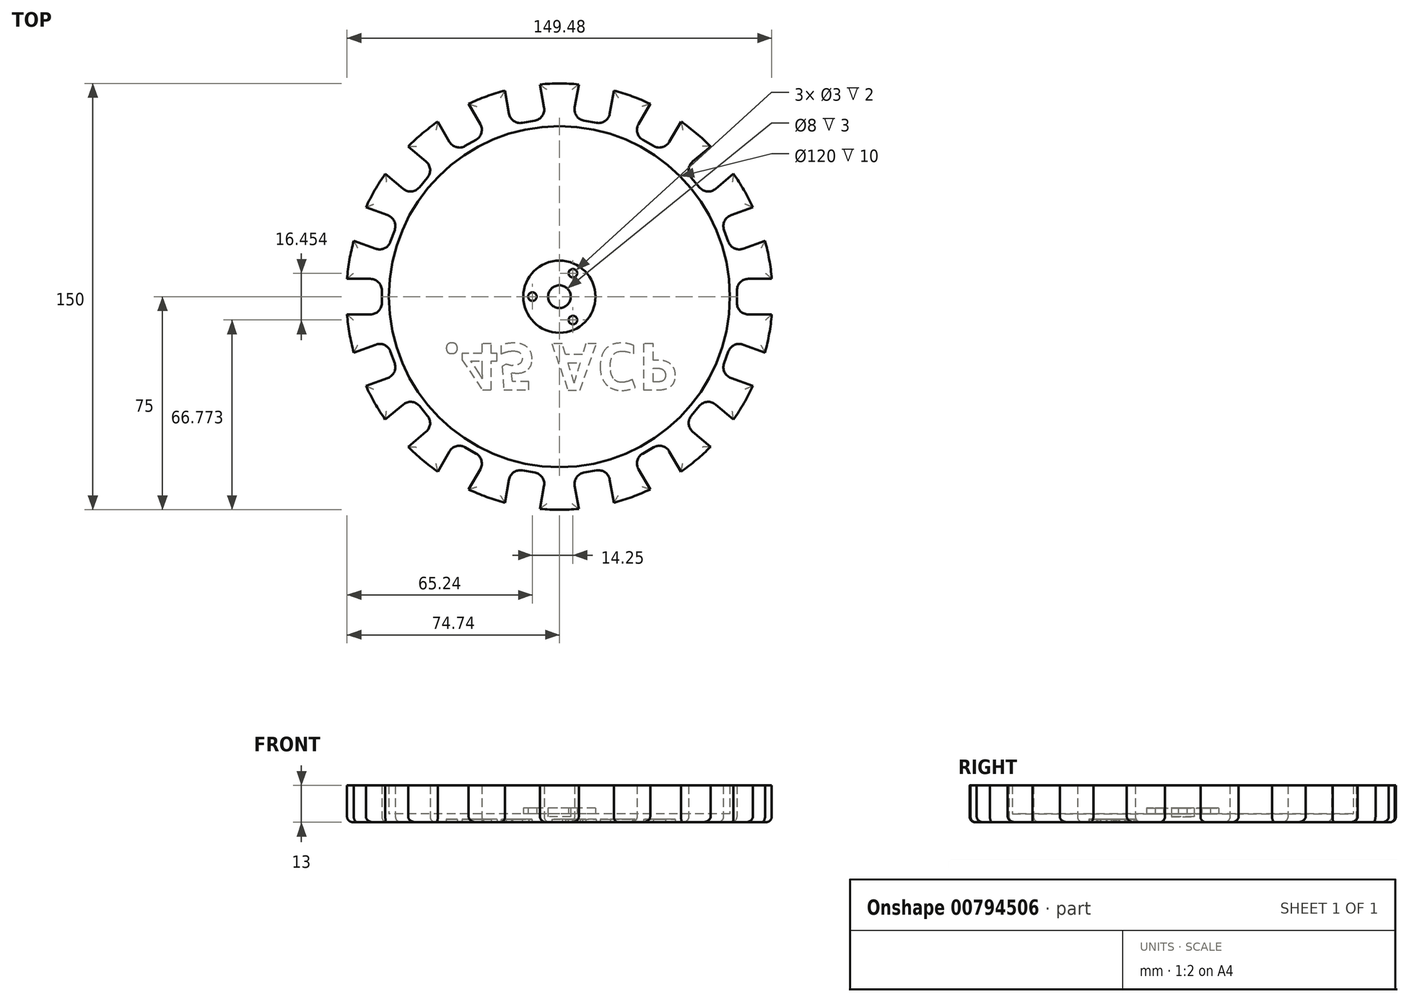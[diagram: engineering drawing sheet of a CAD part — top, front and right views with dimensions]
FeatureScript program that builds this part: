
annotation { "Feature Type Name" : "Feature", "Feature Type Description" : "" }
export const myFeature = defineFeature(function(context is Context, id is Id, definition is map)
    precondition{}
    {
        {
            var Q0;
            Q0=qCreatedBy(makeId("Top.planeOp"),FACE);
            var sketch = newSketch(context, id + "F0", { "sketchPlane" : qUnion([Q0])});
            skCircle(sketch, "E0", {"center": v(0, 0) * mm, "radius": 75 * mm});
            skCircle(sketch, "E1", {"center": v(0, 0) * mm, "radius": 60 * mm});
            skLineSegment(sketch, "E2", {"start": v(0, 0) * mm, "end": v(-124.02, 0) * mm, "construction": true});
            skPoint(sketch, "E3", {"position": v(-75, 0) * mm});
            skLineSegment(sketch, "E4.bottom", {"start": v(-75, -6.25) * mm, "end": v(-66.5, -6.25) * mm});
            skLineSegment(sketch, "E4.top", {"start": v(-75, 6.25) * mm, "end": v(-66.5, 6.25) * mm});
            skLineSegment(sketch, "E4.left", {"start": v(-75, -6.25) * mm, "end": v(-75, 6.25) * mm});
            skLineSegment(sketch, "E4.right", {"start": v(-62.5, -2.25) * mm, "end": v(-62.5, 2.25) * mm});
            skPoint(sketch, "E4.middle", {"position": v(-68.75, 0) * mm});
            skPoint(sketch, "E5.visualSharp", {"position": v(-62.5, 6.25) * mm});
            skArc(sketch, "E5.filletArc", {"start": v(-62.5, 2.25) * mm, "mid": v(-63.67, 5.08) * mm, "end": v(-66.5, 6.25) * mm});
            skPoint(sketch, "E6.visualSharp", {"position": v(-62.5, -6.25) * mm});
            skArc(sketch, "E6.filletArc", {"start": v(-66.5, -6.25) * mm, "mid": v(-63.67, -5.08) * mm, "end": v(-62.5, -2.25) * mm});
            skPoint(sketch, "E7.center", {"position": v(1.56, 0) * mm});
            skCircle(sketch, "E8", {"center": v(0, 0) * mm, "radius": 4 * mm});
            skCircle(sketch, "E9", {"center": v(0, 0) * mm, "radius": 12.7 * mm});
            skCircle(sketch, "E10", {"center": v(0, 0) * mm, "radius": 9.5 * mm, "construction": true});
            skCircle(sketch, "E11", {"center": v(-9.5, 0) * mm, "radius": 1.5 * mm});
            skCircle(sketch, "E12.1.0", {"center": v(-4.75, -8.23) * mm, "radius": 1.5 * mm});
            skCircle(sketch, "E12.2.0", {"center": v(4.75, -8.23) * mm, "radius": 1.5 * mm});
            skCircle(sketch, "E12.3.0", {"center": v(9.5, 0) * mm, "radius": 1.5 * mm});
            skCircle(sketch, "E12.4.0", {"center": v(4.75, 8.23) * mm, "radius": 1.5 * mm});
            skCircle(sketch, "E12.5.0", {"center": v(-4.75, 8.23) * mm, "radius": 1.5 * mm});
            skPoint(sketch, "E13.1.0", {"position": v(-60.87, -15.5) * mm});
            skPoint(sketch, "E13.1.1", {"position": v(-70.48, -25.65) * mm});
            skPoint(sketch, "E13.1.2", {"position": v(-56.6, -27.25) * mm});
            skPoint(sketch, "E13.1.3", {"position": v(-64.6, -23.51) * mm});
            skArc(sketch, "E13.1.4", {"start": v(-60.35, -28.62) * mm, "mid": v(-58.1, -26.55) * mm, "end": v(-57.96, -23.5) * mm});
            skArc(sketch, "E13.1.5", {"start": v(-59.5, -19.26) * mm, "mid": v(-61.57, -17) * mm, "end": v(-64.63, -16.87) * mm});
            skLineSegment(sketch, "E13.1.6", {"start": v(-68.34, -31.52) * mm, "end": v(-72.61, -19.78) * mm});
            skLineSegment(sketch, "E13.1.7", {"start": v(-57.96, -23.5) * mm, "end": v(-59.5, -19.26) * mm});
            skLineSegment(sketch, "E13.1.8", {"start": v(-72.61, -19.78) * mm, "end": v(-64.63, -16.87) * mm});
            skLineSegment(sketch, "E13.1.9", {"start": v(-68.34, -31.52) * mm, "end": v(-60.35, -28.62) * mm});
            skPoint(sketch, "E13.2.0", {"position": v(-51.9, -35.39) * mm});
            skPoint(sketch, "E13.2.1", {"position": v(-57.45, -48.2) * mm});
            skPoint(sketch, "E13.2.2", {"position": v(-43.86, -44.96) * mm});
            skPoint(sketch, "E13.2.3", {"position": v(-52.67, -44.2) * mm});
            skArc(sketch, "E13.2.4", {"start": v(-46.92, -47.53) * mm, "mid": v(-45.51, -44.82) * mm, "end": v(-46.43, -41.9) * mm});
            skArc(sketch, "E13.2.5", {"start": v(-49.32, -38.45) * mm, "mid": v(-52.04, -37.04) * mm, "end": v(-54.96, -37.96) * mm});
            skLineSegment(sketch, "E13.2.6", {"start": v(-53.44, -53) * mm, "end": v(-61.47, -43.42) * mm});
            skLineSegment(sketch, "E13.2.7", {"start": v(-46.43, -41.9) * mm, "end": v(-49.32, -38.45) * mm});
            skLineSegment(sketch, "E13.2.8", {"start": v(-61.47, -43.42) * mm, "end": v(-54.96, -37.96) * mm});
            skLineSegment(sketch, "E13.2.9", {"start": v(-53.44, -53) * mm, "end": v(-46.92, -47.53) * mm});
            skPoint(sketch, "E13.3.0", {"position": v(-36.66, -51) * mm});
            skPoint(sketch, "E13.3.1", {"position": v(-37.5, -64.95) * mm});
            skPoint(sketch, "E13.3.2", {"position": v(-25.84, -57.25) * mm});
            skPoint(sketch, "E13.3.3", {"position": v(-34.38, -59.54) * mm});
            skArc(sketch, "E13.3.4", {"start": v(-27.84, -60.72) * mm, "mid": v(-27.44, -57.68) * mm, "end": v(-29.3, -55.25) * mm});
            skArc(sketch, "E13.3.5", {"start": v(-33.2, -53) * mm, "mid": v(-36.23, -52.6) * mm, "end": v(-38.66, -54.47) * mm});
            skLineSegment(sketch, "E13.3.6", {"start": v(-32.09, -68.08) * mm, "end": v(-42.91, -61.83) * mm});
            skLineSegment(sketch, "E13.3.7", {"start": v(-29.3, -55.25) * mm, "end": v(-33.2, -53) * mm});
            skLineSegment(sketch, "E13.3.8", {"start": v(-42.91, -61.83) * mm, "end": v(-38.66, -54.47) * mm});
            skLineSegment(sketch, "E13.3.9", {"start": v(-32.09, -68.08) * mm, "end": v(-27.84, -60.72) * mm});
            skPoint(sketch, "E13.4.0", {"position": v(-17, -60.47) * mm});
            skPoint(sketch, "E13.4.1", {"position": v(-13.02, -73.86) * mm});
            skPoint(sketch, "E13.4.2", {"position": v(-4.7, -62.64) * mm});
            skPoint(sketch, "E13.4.3", {"position": v(-11.94, -67.7) * mm});
            skArc(sketch, "E13.4.4", {"start": v(-5.4, -66.58) * mm, "mid": v(-6.06, -63.59) * mm, "end": v(-8.64, -61.94) * mm});
            skArc(sketch, "E13.4.5", {"start": v(-13.07, -61.16) * mm, "mid": v(-16.06, -61.82) * mm, "end": v(-17.7, -64.4) * mm});
            skLineSegment(sketch, "E13.4.6", {"start": v(-6.87, -74.95) * mm, "end": v(-19.18, -72.78) * mm});
            skLineSegment(sketch, "E13.4.7", {"start": v(-8.64, -61.94) * mm, "end": v(-13.07, -61.16) * mm});
            skLineSegment(sketch, "E13.4.8", {"start": v(-19.18, -72.78) * mm, "end": v(-17.7, -64.4) * mm});
            skLineSegment(sketch, "E13.4.9", {"start": v(-6.87, -74.95) * mm, "end": v(-5.4, -66.58) * mm});
            skPoint(sketch, "E13.5.0", {"position": v(4.7, -62.64) * mm});
            skPoint(sketch, "E13.5.1", {"position": v(13.02, -73.86) * mm});
            skPoint(sketch, "E13.5.2", {"position": v(17, -60.47) * mm});
            skPoint(sketch, "E13.5.3", {"position": v(11.94, -67.7) * mm});
            skArc(sketch, "E13.5.4", {"start": v(17.7, -64.4) * mm, "mid": v(16.06, -61.82) * mm, "end": v(13.07, -61.16) * mm});
            skArc(sketch, "E13.5.5", {"start": v(8.64, -61.94) * mm, "mid": v(6.06, -63.59) * mm, "end": v(5.4, -66.58) * mm});
            skLineSegment(sketch, "E13.5.6", {"start": v(19.18, -72.78) * mm, "end": v(6.87, -74.95) * mm});
            skLineSegment(sketch, "E13.5.7", {"start": v(13.07, -61.16) * mm, "end": v(8.64, -61.94) * mm});
            skLineSegment(sketch, "E13.5.8", {"start": v(6.87, -74.95) * mm, "end": v(5.4, -66.58) * mm});
            skLineSegment(sketch, "E13.5.9", {"start": v(19.18, -72.78) * mm, "end": v(17.7, -64.4) * mm});
            skPoint(sketch, "E13.6.0", {"position": v(25.84, -57.25) * mm});
            skPoint(sketch, "E13.6.1", {"position": v(37.5, -64.95) * mm});
            skPoint(sketch, "E13.6.2", {"position": v(36.66, -51) * mm});
            skPoint(sketch, "E13.6.3", {"position": v(34.37, -59.54) * mm});
            skArc(sketch, "E13.6.4", {"start": v(38.66, -54.47) * mm, "mid": v(36.23, -52.6) * mm, "end": v(33.2, -53) * mm});
            skArc(sketch, "E13.6.5", {"start": v(29.3, -55.25) * mm, "mid": v(27.44, -57.68) * mm, "end": v(27.84, -60.72) * mm});
            skLineSegment(sketch, "E13.6.6", {"start": v(42.91, -61.83) * mm, "end": v(32.09, -68.08) * mm});
            skLineSegment(sketch, "E13.6.7", {"start": v(33.2, -53) * mm, "end": v(29.3, -55.25) * mm});
            skLineSegment(sketch, "E13.6.8", {"start": v(32.09, -68.08) * mm, "end": v(27.84, -60.72) * mm});
            skLineSegment(sketch, "E13.6.9", {"start": v(42.91, -61.83) * mm, "end": v(38.66, -54.47) * mm});
            skPoint(sketch, "E13.7.0", {"position": v(43.86, -44.96) * mm});
            skPoint(sketch, "E13.7.1", {"position": v(57.45, -48.2) * mm});
            skPoint(sketch, "E13.7.2", {"position": v(51.9, -35.39) * mm});
            skPoint(sketch, "E13.7.3", {"position": v(52.67, -44.2) * mm});
            skArc(sketch, "E13.7.4", {"start": v(54.96, -37.96) * mm, "mid": v(52.04, -37.04) * mm, "end": v(49.32, -38.45) * mm});
            skArc(sketch, "E13.7.5", {"start": v(46.43, -41.9) * mm, "mid": v(45.51, -44.82) * mm, "end": v(46.92, -47.53) * mm});
            skLineSegment(sketch, "E13.7.6", {"start": v(61.47, -43.42) * mm, "end": v(53.44, -53) * mm});
            skLineSegment(sketch, "E13.7.7", {"start": v(49.32, -38.45) * mm, "end": v(46.43, -41.9) * mm});
            skLineSegment(sketch, "E13.7.8", {"start": v(53.44, -53) * mm, "end": v(46.92, -47.53) * mm});
            skLineSegment(sketch, "E13.7.9", {"start": v(61.47, -43.42) * mm, "end": v(54.96, -37.96) * mm});
            skPoint(sketch, "E13.8.0", {"position": v(56.6, -27.25) * mm});
            skPoint(sketch, "E13.8.1", {"position": v(70.48, -25.65) * mm});
            skPoint(sketch, "E13.8.2", {"position": v(60.87, -15.5) * mm});
            skPoint(sketch, "E13.8.3", {"position": v(64.6, -23.51) * mm});
            skArc(sketch, "E13.8.4", {"start": v(64.63, -16.87) * mm, "mid": v(61.57, -17) * mm, "end": v(59.5, -19.26) * mm});
            skArc(sketch, "E13.8.5", {"start": v(57.96, -23.5) * mm, "mid": v(58.1, -26.55) * mm, "end": v(60.35, -28.62) * mm});
            skLineSegment(sketch, "E13.8.6", {"start": v(72.61, -19.78) * mm, "end": v(68.34, -31.52) * mm});
            skLineSegment(sketch, "E13.8.7", {"start": v(59.5, -19.26) * mm, "end": v(57.96, -23.5) * mm});
            skLineSegment(sketch, "E13.8.8", {"start": v(68.34, -31.52) * mm, "end": v(60.35, -28.62) * mm});
            skLineSegment(sketch, "E13.8.9", {"start": v(72.61, -19.78) * mm, "end": v(64.63, -16.87) * mm});
            skPoint(sketch, "E13.9.0", {"position": v(62.5, -6.25) * mm});
            skPoint(sketch, "E13.9.1", {"position": v(75, 0) * mm});
            skPoint(sketch, "E13.9.2", {"position": v(62.5, 6.25) * mm});
            skPoint(sketch, "E13.9.3", {"position": v(68.75, 0) * mm});
            skArc(sketch, "E13.9.4", {"start": v(66.5, 6.25) * mm, "mid": v(63.67, 5.08) * mm, "end": v(62.5, 2.25) * mm});
            skArc(sketch, "E13.9.5", {"start": v(62.5, -2.25) * mm, "mid": v(63.67, -5.08) * mm, "end": v(66.5, -6.25) * mm});
            skLineSegment(sketch, "E13.9.6", {"start": v(75, 6.25) * mm, "end": v(75, -6.25) * mm});
            skLineSegment(sketch, "E13.9.7", {"start": v(62.5, 2.25) * mm, "end": v(62.5, -2.25) * mm});
            skLineSegment(sketch, "E13.9.8", {"start": v(75, -6.25) * mm, "end": v(66.5, -6.25) * mm});
            skLineSegment(sketch, "E13.9.9", {"start": v(75, 6.25) * mm, "end": v(66.5, 6.25) * mm});
            skPoint(sketch, "E13.10.0", {"position": v(60.87, 15.5) * mm});
            skPoint(sketch, "E13.10.1", {"position": v(70.48, 25.65) * mm});
            skPoint(sketch, "E13.10.2", {"position": v(56.6, 27.25) * mm});
            skPoint(sketch, "E13.10.3", {"position": v(64.6, 23.51) * mm});
            skArc(sketch, "E13.10.4", {"start": v(60.35, 28.62) * mm, "mid": v(58.1, 26.55) * mm, "end": v(57.96, 23.5) * mm});
            skArc(sketch, "E13.10.5", {"start": v(59.5, 19.26) * mm, "mid": v(61.57, 17) * mm, "end": v(64.63, 16.87) * mm});
            skLineSegment(sketch, "E13.10.6", {"start": v(68.34, 31.52) * mm, "end": v(72.61, 19.78) * mm});
            skLineSegment(sketch, "E13.10.7", {"start": v(57.96, 23.5) * mm, "end": v(59.5, 19.26) * mm});
            skLineSegment(sketch, "E13.10.8", {"start": v(72.61, 19.78) * mm, "end": v(64.63, 16.87) * mm});
            skLineSegment(sketch, "E13.10.9", {"start": v(68.34, 31.52) * mm, "end": v(60.35, 28.62) * mm});
            skPoint(sketch, "E13.11.0", {"position": v(51.9, 35.39) * mm});
            skPoint(sketch, "E13.11.1", {"position": v(57.45, 48.2) * mm});
            skPoint(sketch, "E13.11.2", {"position": v(43.86, 44.96) * mm});
            skPoint(sketch, "E13.11.3", {"position": v(52.67, 44.2) * mm});
            skArc(sketch, "E13.11.4", {"start": v(46.92, 47.53) * mm, "mid": v(45.51, 44.82) * mm, "end": v(46.43, 41.9) * mm});
            skArc(sketch, "E13.11.5", {"start": v(49.32, 38.45) * mm, "mid": v(52.04, 37.04) * mm, "end": v(54.96, 37.96) * mm});
            skLineSegment(sketch, "E13.11.6", {"start": v(53.44, 53) * mm, "end": v(61.47, 43.42) * mm});
            skLineSegment(sketch, "E13.11.7", {"start": v(46.43, 41.9) * mm, "end": v(49.32, 38.45) * mm});
            skLineSegment(sketch, "E13.11.8", {"start": v(61.47, 43.42) * mm, "end": v(54.96, 37.96) * mm});
            skLineSegment(sketch, "E13.11.9", {"start": v(53.44, 53) * mm, "end": v(46.92, 47.53) * mm});
            skPoint(sketch, "E13.12.0", {"position": v(36.66, 51) * mm});
            skPoint(sketch, "E13.12.1", {"position": v(37.5, 64.95) * mm});
            skPoint(sketch, "E13.12.2", {"position": v(25.84, 57.25) * mm});
            skPoint(sketch, "E13.12.3", {"position": v(34.38, 59.54) * mm});
            skArc(sketch, "E13.12.4", {"start": v(27.84, 60.72) * mm, "mid": v(27.44, 57.68) * mm, "end": v(29.3, 55.25) * mm});
            skArc(sketch, "E13.12.5", {"start": v(33.2, 53) * mm, "mid": v(36.23, 52.6) * mm, "end": v(38.66, 54.47) * mm});
            skLineSegment(sketch, "E13.12.6", {"start": v(32.09, 68.08) * mm, "end": v(42.91, 61.83) * mm});
            skLineSegment(sketch, "E13.12.7", {"start": v(29.3, 55.25) * mm, "end": v(33.2, 53) * mm});
            skLineSegment(sketch, "E13.12.8", {"start": v(42.91, 61.83) * mm, "end": v(38.66, 54.47) * mm});
            skLineSegment(sketch, "E13.12.9", {"start": v(32.09, 68.08) * mm, "end": v(27.84, 60.72) * mm});
            skPoint(sketch, "E13.13.0", {"position": v(17, 60.47) * mm});
            skPoint(sketch, "E13.13.1", {"position": v(13.02, 73.86) * mm});
            skPoint(sketch, "E13.13.2", {"position": v(4.7, 62.64) * mm});
            skPoint(sketch, "E13.13.3", {"position": v(11.94, 67.7) * mm});
            skArc(sketch, "E13.13.4", {"start": v(5.4, 66.58) * mm, "mid": v(6.06, 63.59) * mm, "end": v(8.64, 61.94) * mm});
            skArc(sketch, "E13.13.5", {"start": v(13.07, 61.16) * mm, "mid": v(16.06, 61.82) * mm, "end": v(17.7, 64.4) * mm});
            skLineSegment(sketch, "E13.13.6", {"start": v(6.87, 74.95) * mm, "end": v(19.18, 72.78) * mm});
            skLineSegment(sketch, "E13.13.7", {"start": v(8.64, 61.94) * mm, "end": v(13.07, 61.16) * mm});
            skLineSegment(sketch, "E13.13.8", {"start": v(19.18, 72.78) * mm, "end": v(17.7, 64.4) * mm});
            skLineSegment(sketch, "E13.13.9", {"start": v(6.87, 74.95) * mm, "end": v(5.4, 66.58) * mm});
            skPoint(sketch, "E13.14.0", {"position": v(-4.7, 62.64) * mm});
            skPoint(sketch, "E13.14.1", {"position": v(-13.02, 73.86) * mm});
            skPoint(sketch, "E13.14.2", {"position": v(-17, 60.47) * mm});
            skPoint(sketch, "E13.14.3", {"position": v(-11.94, 67.7) * mm});
            skArc(sketch, "E13.14.4", {"start": v(-17.7, 64.4) * mm, "mid": v(-16.06, 61.82) * mm, "end": v(-13.07, 61.16) * mm});
            skArc(sketch, "E13.14.5", {"start": v(-8.64, 61.94) * mm, "mid": v(-6.06, 63.59) * mm, "end": v(-5.4, 66.58) * mm});
            skLineSegment(sketch, "E13.14.6", {"start": v(-19.18, 72.78) * mm, "end": v(-6.87, 74.95) * mm});
            skLineSegment(sketch, "E13.14.7", {"start": v(-13.07, 61.16) * mm, "end": v(-8.64, 61.94) * mm});
            skLineSegment(sketch, "E13.14.8", {"start": v(-6.87, 74.95) * mm, "end": v(-5.4, 66.58) * mm});
            skLineSegment(sketch, "E13.14.9", {"start": v(-19.18, 72.78) * mm, "end": v(-17.7, 64.4) * mm});
            skPoint(sketch, "E13.15.0", {"position": v(-25.84, 57.25) * mm});
            skPoint(sketch, "E13.15.1", {"position": v(-37.5, 64.95) * mm});
            skPoint(sketch, "E13.15.2", {"position": v(-36.66, 51) * mm});
            skPoint(sketch, "E13.15.3", {"position": v(-34.37, 59.54) * mm});
            skArc(sketch, "E13.15.4", {"start": v(-38.66, 54.47) * mm, "mid": v(-36.23, 52.6) * mm, "end": v(-33.2, 53) * mm});
            skArc(sketch, "E13.15.5", {"start": v(-29.3, 55.25) * mm, "mid": v(-27.44, 57.68) * mm, "end": v(-27.84, 60.72) * mm});
            skLineSegment(sketch, "E13.15.6", {"start": v(-42.91, 61.83) * mm, "end": v(-32.09, 68.08) * mm});
            skLineSegment(sketch, "E13.15.7", {"start": v(-33.2, 53) * mm, "end": v(-29.3, 55.25) * mm});
            skLineSegment(sketch, "E13.15.8", {"start": v(-32.09, 68.08) * mm, "end": v(-27.84, 60.72) * mm});
            skLineSegment(sketch, "E13.15.9", {"start": v(-42.91, 61.83) * mm, "end": v(-38.66, 54.47) * mm});
            skPoint(sketch, "E13.16.0", {"position": v(-43.86, 44.96) * mm});
            skPoint(sketch, "E13.16.1", {"position": v(-57.45, 48.2) * mm});
            skPoint(sketch, "E13.16.2", {"position": v(-51.9, 35.39) * mm});
            skPoint(sketch, "E13.16.3", {"position": v(-52.67, 44.2) * mm});
            skArc(sketch, "E13.16.4", {"start": v(-54.96, 37.96) * mm, "mid": v(-52.04, 37.04) * mm, "end": v(-49.32, 38.45) * mm});
            skArc(sketch, "E13.16.5", {"start": v(-46.43, 41.9) * mm, "mid": v(-45.51, 44.82) * mm, "end": v(-46.92, 47.53) * mm});
            skLineSegment(sketch, "E13.16.6", {"start": v(-61.47, 43.42) * mm, "end": v(-53.44, 53) * mm});
            skLineSegment(sketch, "E13.16.7", {"start": v(-49.32, 38.45) * mm, "end": v(-46.43, 41.9) * mm});
            skLineSegment(sketch, "E13.16.8", {"start": v(-53.44, 53) * mm, "end": v(-46.92, 47.53) * mm});
            skLineSegment(sketch, "E13.16.9", {"start": v(-61.47, 43.42) * mm, "end": v(-54.96, 37.96) * mm});
            skPoint(sketch, "E13.17.0", {"position": v(-56.6, 27.25) * mm});
            skPoint(sketch, "E13.17.1", {"position": v(-70.48, 25.65) * mm});
            skPoint(sketch, "E13.17.2", {"position": v(-60.87, 15.5) * mm});
            skPoint(sketch, "E13.17.3", {"position": v(-64.6, 23.51) * mm});
            skArc(sketch, "E13.17.4", {"start": v(-64.63, 16.87) * mm, "mid": v(-61.57, 17) * mm, "end": v(-59.5, 19.26) * mm});
            skArc(sketch, "E13.17.5", {"start": v(-57.96, 23.5) * mm, "mid": v(-58.1, 26.55) * mm, "end": v(-60.35, 28.62) * mm});
            skLineSegment(sketch, "E13.17.6", {"start": v(-72.61, 19.78) * mm, "end": v(-68.34, 31.52) * mm});
            skLineSegment(sketch, "E13.17.7", {"start": v(-59.5, 19.26) * mm, "end": v(-57.96, 23.5) * mm});
            skLineSegment(sketch, "E13.17.8", {"start": v(-68.34, 31.52) * mm, "end": v(-60.35, 28.62) * mm});
            skLineSegment(sketch, "E13.17.9", {"start": v(-72.61, 19.78) * mm, "end": v(-64.63, 16.87) * mm});
            skSolve(sketch);
        }
        {
            var Q0;
            Q0=makeQuery(id+"F0.imprint","IMPRINT",FACE,{"disambiguationData":[TD([[makeQuery(id+"F0.imprint","IMPRINT",EDGE,{"derivedFrom":sQuery(id+"F0.wireOp",EDGE,"E1")}),1.0]])]});
            var Q1;
            Q1=makeQuery(id+"F0.imprint","IMPRINT",FACE,{"disambiguationData":[TD([[makeQuery(id+"F0.imprint","IMPRINT",EDGE,{"derivedFrom":sQuery(id+"F0.wireOp",EDGE,"E8")}),-1.0]])]});
            var Q2;
            Q2=makeQuery(id+"F0.imprint","IMPRINT",FACE,{"disambiguationData":[TD([[makeQuery(id+"F0.imprint","IMPRINT",EDGE,{"derivedFrom":sQuery(id+"F0.wireOp",EDGE,"E12.3.0")}),1.0]])]});
            var Q3;
            Q3=makeQuery(id+"F0.imprint","IMPRINT",FACE,{"disambiguationData":[TD([[makeQuery(id+"F0.imprint","IMPRINT",EDGE,{"derivedFrom":sQuery(id+"F0.wireOp",EDGE,"E12.4.0")}),1.0]])]});
            var Q4;
            Q4=makeQuery(id+"F0.imprint","IMPRINT",FACE,{"disambiguationData":[TD([[makeQuery(id+"F0.imprint","IMPRINT",EDGE,{"derivedFrom":sQuery(id+"F0.wireOp",EDGE,"E12.5.0")}),1.0]])]});
            var Q5;
            Q5=makeQuery(id+"F0.imprint","IMPRINT",FACE,{"disambiguationData":[TD([[makeQuery(id+"F0.imprint","IMPRINT",EDGE,{"derivedFrom":sQuery(id+"F0.wireOp",EDGE,"E11")}),1.0]])]});
            var Q6;
            Q6=makeQuery(id+"F0.imprint","IMPRINT",FACE,{"disambiguationData":[TD([[makeQuery(id+"F0.imprint","IMPRINT",EDGE,{"derivedFrom":sQuery(id+"F0.wireOp",EDGE,"E12.1.0")}),1.0]])]});
            var Q7;
            Q7=makeQuery(id+"F0.imprint","IMPRINT",FACE,{"disambiguationData":[TD([[makeQuery(id+"F0.imprint","IMPRINT",EDGE,{"derivedFrom":sQuery(id+"F0.wireOp",EDGE,"E12.2.0")}),1.0]])]});
            extrude(context, id + "F1", {"entities" : qUnion([Q0, Q1, Q2, Q3, Q4, Q5, Q6, Q7]), "depth" : 3 * mm, "offsetDistance" : 25 * mm});
        }
        {
            var Q0;
            Q0=makeQuery(id+"F0.imprint","IMPRINT",FACE,{"disambiguationData":[TD([[makeQuery(id+"F0.imprint","IMPRINT",EDGE,{"derivedFrom":sQuery(id+"F0.wireOp",EDGE,"E1")}),-1.0]])]});
            extrude(context, id + "F2", {"entities" : qUnion([Q0]), "operationType" : NewBodyOperationType.ADD, "depth" : 13 * mm, "offsetDistance" : 25 * mm});
        }
        {
            var Q0;
            Q0=makeQuery(id+"F0.imprint","IMPRINT",FACE,{"disambiguationData":[TD([[makeQuery(id+"F0.imprint","IMPRINT",EDGE,{"derivedFrom":sQuery(id+"F0.wireOp",EDGE,"E8")}),-1.0]])]});
            var Q1;
            Q1=makeQuery(id+"F0.imprint","IMPRINT",FACE,{"disambiguationData":[TD([[makeQuery(id+"F0.imprint","IMPRINT",EDGE,{"derivedFrom":sQuery(id+"F0.wireOp",EDGE,"E12.5.0")}),1.0]])]});
            var Q2;
            Q2=makeQuery(id+"F0.imprint","IMPRINT",FACE,{"disambiguationData":[TD([[makeQuery(id+"F0.imprint","IMPRINT",EDGE,{"derivedFrom":sQuery(id+"F0.wireOp",EDGE,"E12.3.0")}),1.0]])]});
            var Q3;
            Q3=makeQuery(id+"F0.imprint","IMPRINT",FACE,{"disambiguationData":[TD([[makeQuery(id+"F0.imprint","IMPRINT",EDGE,{"derivedFrom":sQuery(id+"F0.wireOp",EDGE,"E12.1.0")}),1.0]])]});
            extrude(context, id + "F3", {"entities" : qUnion([Q0, Q1, Q2, Q3]), "operationType" : NewBodyOperationType.ADD, "depth" : 5 * mm, "offsetDistance" : 25 * mm});
        }
        {
            var Q0;
            Q0=makeQuery(id+"F0.imprint","IMPRINT",FACE,{"disambiguationData":[TD([[makeQuery(id+"F0.imprint","IMPRINT",EDGE,{"derivedFrom":sQuery(id+"F0.wireOp",EDGE,"E8")}),1.0]])]});
            extrude(context, id + "F4", {"entities" : qUnion([Q0]), "operationType" : NewBodyOperationType.ADD, "depth" : 2 * mm, "offsetDistance" : 25 * mm});
        }
        {
            var Q0;
            {var subQ0=sQuery(id+"F0.wireOp",EDGE,"E8");var subQ1=sQuery(id+"F0.wireOp",EDGE,"E1");Q0=makeQuery(id+"F4.boolean.opBoolean","MERGE",FACE,{"derivedFrom":[makeQuery(id+"F2.boolean.opBoolean","MERGE",FACE,{"derivedFrom":[makeQuery(id+"F1.opExtrude","CAP_FACE",FACE,{"disambiguationData":[OSD([subQ1,subQ0])],"isStart":true}),makeQuery(id+"F2.opExtrude","CAP_FACE",FACE,{"disambiguationData":[OSD([sQuery(id+"F0.wireOp",EDGE,"E0"),subQ1,sQuery(id+"F0.wireOp",EDGE,"E4.bottom"),sQuery(id+"F0.wireOp",EDGE,"E4.top"),sQuery(id+"F0.wireOp",EDGE,"E4.right"),sQuery(id+"F0.wireOp",EDGE,"E5.filletArc"),sQuery(id+"F0.wireOp",EDGE,"E6.filletArc"),sQuery(id+"F0.wireOp",EDGE,"E13.1.4"),sQuery(id+"F0.wireOp",EDGE,"E13.1.5"),sQuery(id+"F0.wireOp",EDGE,"E13.1.7"),sQuery(id+"F0.wireOp",EDGE,"E13.1.8"),sQuery(id+"F0.wireOp",EDGE,"E13.1.9"),sQuery(id+"F0.wireOp",EDGE,"E13.2.4"),sQuery(id+"F0.wireOp",EDGE,"E13.2.5"),sQuery(id+"F0.wireOp",EDGE,"E13.2.7"),sQuery(id+"F0.wireOp",EDGE,"E13.2.8"),sQuery(id+"F0.wireOp",EDGE,"E13.2.9"),sQuery(id+"F0.wireOp",EDGE,"E13.3.4"),sQuery(id+"F0.wireOp",EDGE,"E13.3.5"),sQuery(id+"F0.wireOp",EDGE,"E13.3.7"),sQuery(id+"F0.wireOp",EDGE,"E13.3.8"),sQuery(id+"F0.wireOp",EDGE,"E13.3.9"),sQuery(id+"F0.wireOp",EDGE,"E13.4.4"),sQuery(id+"F0.wireOp",EDGE,"E13.4.5"),sQuery(id+"F0.wireOp",EDGE,"E13.4.7"),sQuery(id+"F0.wireOp",EDGE,"E13.4.8"),sQuery(id+"F0.wireOp",EDGE,"E13.4.9"),sQuery(id+"F0.wireOp",EDGE,"E13.5.4"),sQuery(id+"F0.wireOp",EDGE,"E13.5.5"),sQuery(id+"F0.wireOp",EDGE,"E13.5.7"),sQuery(id+"F0.wireOp",EDGE,"E13.5.8"),sQuery(id+"F0.wireOp",EDGE,"E13.5.9"),sQuery(id+"F0.wireOp",EDGE,"E13.6.4"),sQuery(id+"F0.wireOp",EDGE,"E13.6.5"),sQuery(id+"F0.wireOp",EDGE,"E13.6.7"),sQuery(id+"F0.wireOp",EDGE,"E13.6.8"),sQuery(id+"F0.wireOp",EDGE,"E13.6.9"),sQuery(id+"F0.wireOp",EDGE,"E13.7.4"),sQuery(id+"F0.wireOp",EDGE,"E13.7.5"),sQuery(id+"F0.wireOp",EDGE,"E13.7.7"),sQuery(id+"F0.wireOp",EDGE,"E13.7.8"),sQuery(id+"F0.wireOp",EDGE,"E13.7.9"),sQuery(id+"F0.wireOp",EDGE,"E13.8.4"),sQuery(id+"F0.wireOp",EDGE,"E13.8.5"),sQuery(id+"F0.wireOp",EDGE,"E13.8.7"),sQuery(id+"F0.wireOp",EDGE,"E13.8.8"),sQuery(id+"F0.wireOp",EDGE,"E13.8.9"),sQuery(id+"F0.wireOp",EDGE,"E13.9.4"),sQuery(id+"F0.wireOp",EDGE,"E13.9.5"),sQuery(id+"F0.wireOp",EDGE,"E13.9.7"),sQuery(id+"F0.wireOp",EDGE,"E13.9.8"),sQuery(id+"F0.wireOp",EDGE,"E13.9.9"),sQuery(id+"F0.wireOp",EDGE,"E13.10.4"),sQuery(id+"F0.wireOp",EDGE,"E13.10.5"),sQuery(id+"F0.wireOp",EDGE,"E13.10.7"),sQuery(id+"F0.wireOp",EDGE,"E13.10.8"),sQuery(id+"F0.wireOp",EDGE,"E13.10.9"),sQuery(id+"F0.wireOp",EDGE,"E13.11.4"),sQuery(id+"F0.wireOp",EDGE,"E13.11.5"),sQuery(id+"F0.wireOp",EDGE,"E13.11.7"),sQuery(id+"F0.wireOp",EDGE,"E13.11.8"),sQuery(id+"F0.wireOp",EDGE,"E13.11.9"),sQuery(id+"F0.wireOp",EDGE,"E13.12.4"),sQuery(id+"F0.wireOp",EDGE,"E13.12.5"),sQuery(id+"F0.wireOp",EDGE,"E13.12.7"),sQuery(id+"F0.wireOp",EDGE,"E13.12.8"),sQuery(id+"F0.wireOp",EDGE,"E13.12.9"),sQuery(id+"F0.wireOp",EDGE,"E13.13.4"),sQuery(id+"F0.wireOp",EDGE,"E13.13.5"),sQuery(id+"F0.wireOp",EDGE,"E13.13.7"),sQuery(id+"F0.wireOp",EDGE,"E13.13.8"),sQuery(id+"F0.wireOp",EDGE,"E13.13.9"),sQuery(id+"F0.wireOp",EDGE,"E13.14.4"),sQuery(id+"F0.wireOp",EDGE,"E13.14.5"),sQuery(id+"F0.wireOp",EDGE,"E13.14.7"),sQuery(id+"F0.wireOp",EDGE,"E13.14.8"),sQuery(id+"F0.wireOp",EDGE,"E13.14.9"),sQuery(id+"F0.wireOp",EDGE,"E13.15.4"),sQuery(id+"F0.wireOp",EDGE,"E13.15.5"),sQuery(id+"F0.wireOp",EDGE,"E13.15.7"),sQuery(id+"F0.wireOp",EDGE,"E13.15.8"),sQuery(id+"F0.wireOp",EDGE,"E13.15.9"),sQuery(id+"F0.wireOp",EDGE,"E13.16.4"),sQuery(id+"F0.wireOp",EDGE,"E13.16.5"),sQuery(id+"F0.wireOp",EDGE,"E13.16.7"),sQuery(id+"F0.wireOp",EDGE,"E13.16.8"),sQuery(id+"F0.wireOp",EDGE,"E13.16.9"),sQuery(id+"F0.wireOp",EDGE,"E13.17.4"),sQuery(id+"F0.wireOp",EDGE,"E13.17.5"),sQuery(id+"F0.wireOp",EDGE,"E13.17.7"),sQuery(id+"F0.wireOp",EDGE,"E13.17.8"),sQuery(id+"F0.wireOp",EDGE,"E13.17.9")])],"isStart":true})]}),makeQuery(id+"F4.opExtrude","CAP_FACE",FACE,{"disambiguationData":[OSD([subQ0])],"isStart":true})]});}
            fillet(context, id + "F5", {"entities" : qUnion([Q0]), "radius" : 2 * mm, "tangentPropagation" : true, "allowEdgeOverflow" : false});
        }
        {
            var Q0;
            {var subQ0=sQuery(id+"F0.wireOp",EDGE,"E8");var subQ1=sQuery(id+"F0.wireOp",EDGE,"E1");Q0=makeQuery(id+"F4.boolean.opBoolean","MERGE",FACE,{"derivedFrom":[makeQuery(id+"F2.boolean.opBoolean","MERGE",FACE,{"derivedFrom":[makeQuery(id+"F1.opExtrude","CAP_FACE",FACE,{"disambiguationData":[OSD([subQ1,subQ0])],"isStart":true}),makeQuery(id+"F2.opExtrude","CAP_FACE",FACE,{"disambiguationData":[OSD([sQuery(id+"F0.wireOp",EDGE,"E0"),subQ1,sQuery(id+"F0.wireOp",EDGE,"E4.bottom"),sQuery(id+"F0.wireOp",EDGE,"E4.top"),sQuery(id+"F0.wireOp",EDGE,"E4.right"),sQuery(id+"F0.wireOp",EDGE,"E5.filletArc"),sQuery(id+"F0.wireOp",EDGE,"E6.filletArc"),sQuery(id+"F0.wireOp",EDGE,"E13.1.4"),sQuery(id+"F0.wireOp",EDGE,"E13.1.5"),sQuery(id+"F0.wireOp",EDGE,"E13.1.7"),sQuery(id+"F0.wireOp",EDGE,"E13.1.8"),sQuery(id+"F0.wireOp",EDGE,"E13.1.9"),sQuery(id+"F0.wireOp",EDGE,"E13.2.4"),sQuery(id+"F0.wireOp",EDGE,"E13.2.5"),sQuery(id+"F0.wireOp",EDGE,"E13.2.7"),sQuery(id+"F0.wireOp",EDGE,"E13.2.8"),sQuery(id+"F0.wireOp",EDGE,"E13.2.9"),sQuery(id+"F0.wireOp",EDGE,"E13.3.4"),sQuery(id+"F0.wireOp",EDGE,"E13.3.5"),sQuery(id+"F0.wireOp",EDGE,"E13.3.7"),sQuery(id+"F0.wireOp",EDGE,"E13.3.8"),sQuery(id+"F0.wireOp",EDGE,"E13.3.9"),sQuery(id+"F0.wireOp",EDGE,"E13.4.4"),sQuery(id+"F0.wireOp",EDGE,"E13.4.5"),sQuery(id+"F0.wireOp",EDGE,"E13.4.7"),sQuery(id+"F0.wireOp",EDGE,"E13.4.8"),sQuery(id+"F0.wireOp",EDGE,"E13.4.9"),sQuery(id+"F0.wireOp",EDGE,"E13.5.4"),sQuery(id+"F0.wireOp",EDGE,"E13.5.5"),sQuery(id+"F0.wireOp",EDGE,"E13.5.7"),sQuery(id+"F0.wireOp",EDGE,"E13.5.8"),sQuery(id+"F0.wireOp",EDGE,"E13.5.9"),sQuery(id+"F0.wireOp",EDGE,"E13.6.4"),sQuery(id+"F0.wireOp",EDGE,"E13.6.5"),sQuery(id+"F0.wireOp",EDGE,"E13.6.7"),sQuery(id+"F0.wireOp",EDGE,"E13.6.8"),sQuery(id+"F0.wireOp",EDGE,"E13.6.9"),sQuery(id+"F0.wireOp",EDGE,"E13.7.4"),sQuery(id+"F0.wireOp",EDGE,"E13.7.5"),sQuery(id+"F0.wireOp",EDGE,"E13.7.7"),sQuery(id+"F0.wireOp",EDGE,"E13.7.8"),sQuery(id+"F0.wireOp",EDGE,"E13.7.9"),sQuery(id+"F0.wireOp",EDGE,"E13.8.4"),sQuery(id+"F0.wireOp",EDGE,"E13.8.5"),sQuery(id+"F0.wireOp",EDGE,"E13.8.7"),sQuery(id+"F0.wireOp",EDGE,"E13.8.8"),sQuery(id+"F0.wireOp",EDGE,"E13.8.9"),sQuery(id+"F0.wireOp",EDGE,"E13.9.4"),sQuery(id+"F0.wireOp",EDGE,"E13.9.5"),sQuery(id+"F0.wireOp",EDGE,"E13.9.7"),sQuery(id+"F0.wireOp",EDGE,"E13.9.8"),sQuery(id+"F0.wireOp",EDGE,"E13.9.9"),sQuery(id+"F0.wireOp",EDGE,"E13.10.4"),sQuery(id+"F0.wireOp",EDGE,"E13.10.5"),sQuery(id+"F0.wireOp",EDGE,"E13.10.7"),sQuery(id+"F0.wireOp",EDGE,"E13.10.8"),sQuery(id+"F0.wireOp",EDGE,"E13.10.9"),sQuery(id+"F0.wireOp",EDGE,"E13.11.4"),sQuery(id+"F0.wireOp",EDGE,"E13.11.5"),sQuery(id+"F0.wireOp",EDGE,"E13.11.7"),sQuery(id+"F0.wireOp",EDGE,"E13.11.8"),sQuery(id+"F0.wireOp",EDGE,"E13.11.9"),sQuery(id+"F0.wireOp",EDGE,"E13.12.4"),sQuery(id+"F0.wireOp",EDGE,"E13.12.5"),sQuery(id+"F0.wireOp",EDGE,"E13.12.7"),sQuery(id+"F0.wireOp",EDGE,"E13.12.8"),sQuery(id+"F0.wireOp",EDGE,"E13.12.9"),sQuery(id+"F0.wireOp",EDGE,"E13.13.4"),sQuery(id+"F0.wireOp",EDGE,"E13.13.5"),sQuery(id+"F0.wireOp",EDGE,"E13.13.7"),sQuery(id+"F0.wireOp",EDGE,"E13.13.8"),sQuery(id+"F0.wireOp",EDGE,"E13.13.9"),sQuery(id+"F0.wireOp",EDGE,"E13.14.4"),sQuery(id+"F0.wireOp",EDGE,"E13.14.5"),sQuery(id+"F0.wireOp",EDGE,"E13.14.7"),sQuery(id+"F0.wireOp",EDGE,"E13.14.8"),sQuery(id+"F0.wireOp",EDGE,"E13.14.9"),sQuery(id+"F0.wireOp",EDGE,"E13.15.4"),sQuery(id+"F0.wireOp",EDGE,"E13.15.5"),sQuery(id+"F0.wireOp",EDGE,"E13.15.7"),sQuery(id+"F0.wireOp",EDGE,"E13.15.8"),sQuery(id+"F0.wireOp",EDGE,"E13.15.9"),sQuery(id+"F0.wireOp",EDGE,"E13.16.4"),sQuery(id+"F0.wireOp",EDGE,"E13.16.5"),sQuery(id+"F0.wireOp",EDGE,"E13.16.7"),sQuery(id+"F0.wireOp",EDGE,"E13.16.8"),sQuery(id+"F0.wireOp",EDGE,"E13.16.9"),sQuery(id+"F0.wireOp",EDGE,"E13.17.4"),sQuery(id+"F0.wireOp",EDGE,"E13.17.5"),sQuery(id+"F0.wireOp",EDGE,"E13.17.7"),sQuery(id+"F0.wireOp",EDGE,"E13.17.8"),sQuery(id+"F0.wireOp",EDGE,"E13.17.9")])],"isStart":true})]}),makeQuery(id+"F4.opExtrude","CAP_FACE",FACE,{"disambiguationData":[OSD([subQ0])],"isStart":true})]});}
            var sketch = newSketch(context, id + "F6", { "sketchPlane" : qUnion([Q0])});
            skText(sketch, "E14", { "text": ".45 ACP", "fontName": "OpenSans-Bold.ttf"});
            const initialGuessF6  = {"E14": [-0.04111, 0.01655, 1, 0, 0.0164]};
            skSetInitialGuess(sketch, initialGuessF6);
            skSolve(sketch);
        }
        {
            var Q0;
            Q0 = qSketchRegion(id + "F6", true);
            extrude(context, id + "F7", {"entities" : qUnion([Q0]), "operationType" : NewBodyOperationType.REMOVE, "surfaceOperationType" : NewSurfaceOperationType.ADD, "oppositeDirection" : true, "depth" : 1 * mm, "offsetDistance" : 25 * mm});
        }
    });
